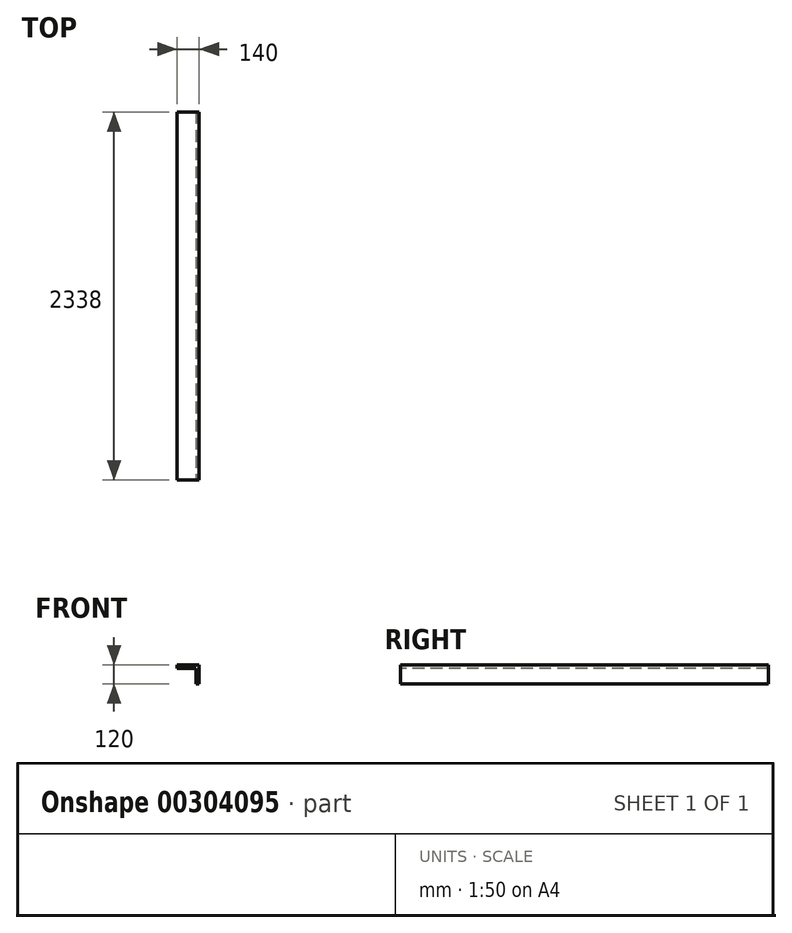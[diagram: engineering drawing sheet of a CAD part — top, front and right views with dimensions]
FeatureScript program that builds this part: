
annotation { "Feature Type Name" : "Feature", "Feature Type Description" : "" }
export const myFeature = defineFeature(function(context is Context, id is Id, definition is map)
    precondition{}
    {
        {
            var Q0;
            Q0=qCreatedBy(makeId("Top.planeOp"),FACE);
            var sketch = newSketch(context, id + "F0", { "sketchPlane" : qUnion([Q0])});
            skLineSegment(sketch, "E0.bottom", {"start": v(-97.05, 1198.8) * mm, "end": v(42.95, 1198.8) * mm});
            skLineSegment(sketch, "E0.top", {"start": v(-97.05, -1139.2) * mm, "end": v(42.95, -1139.2) * mm});
            skLineSegment(sketch, "E0.left", {"start": v(-97.05, 1198.8) * mm, "end": v(-97.05, -1139.2) * mm});
            skLineSegment(sketch, "E0.right", {"start": v(42.95, 1198.8) * mm, "end": v(42.95, -1139.2) * mm});
            skSolve(sketch);
        }
        {
            var Q0;
            Q0=makeQuery(id+"F0.imprint","IMPRINT",FACE,{"disambiguationData":[TD([[makeQuery(id+"F0.imprint","IMPRINT",EDGE,{"derivedFrom":sQuery(id+"F0.wireOp",EDGE,"E0.bottom")}),-1.0]])]});
            extrude(context, id + "F1", {"entities" : qUnion([Q0]), "depth" : 20 * mm, "offsetDistance" : 25 * mm});
        }
        {
            var Q0;
            Q0=makeQuery(id+"F1.opExtrude","CAP_FACE",FACE,{"disambiguationData":[OSD([sQuery(id+"F0.wireOp",EDGE,"E0.bottom"),sQuery(id+"F0.wireOp",EDGE,"E0.top"),sQuery(id+"F0.wireOp",EDGE,"E0.left"),sQuery(id+"F0.wireOp",EDGE,"E0.right")])],"isStart":true});
            var sketch = newSketch(context, id + "F2", { "sketchPlane" : qUnion([Q0])});
            skLineSegment(sketch, "E1.bottom", {"start": v(42.95, -1198.8) * mm, "end": v(22.95, -1198.8) * mm});
            skLineSegment(sketch, "E1.top", {"start": v(42.95, 1139.2) * mm, "end": v(22.95, 1139.2) * mm});
            skLineSegment(sketch, "E1.left", {"start": v(42.95, -1198.8) * mm, "end": v(42.95, 1139.2) * mm});
            skLineSegment(sketch, "E1.right", {"start": v(22.95, -1198.8) * mm, "end": v(22.95, 1139.2) * mm});
            skSolve(sketch);
        }
        {
            var Q0;
            Q0=makeQuery(id+"F2.imprint","IMPRINT",FACE,{"disambiguationData":[TD([[makeQuery(id+"F2.imprint","IMPRINT",EDGE,{"derivedFrom":sQuery(id+"F2.wireOp",EDGE,"E1.bottom")}),1.0]])]});
            extrude(context, id + "F3", {"entities" : qUnion([Q0]), "operationType" : NewBodyOperationType.ADD, "depth" : 100 * mm, "offsetDistance" : 25 * mm});
        }
    });
